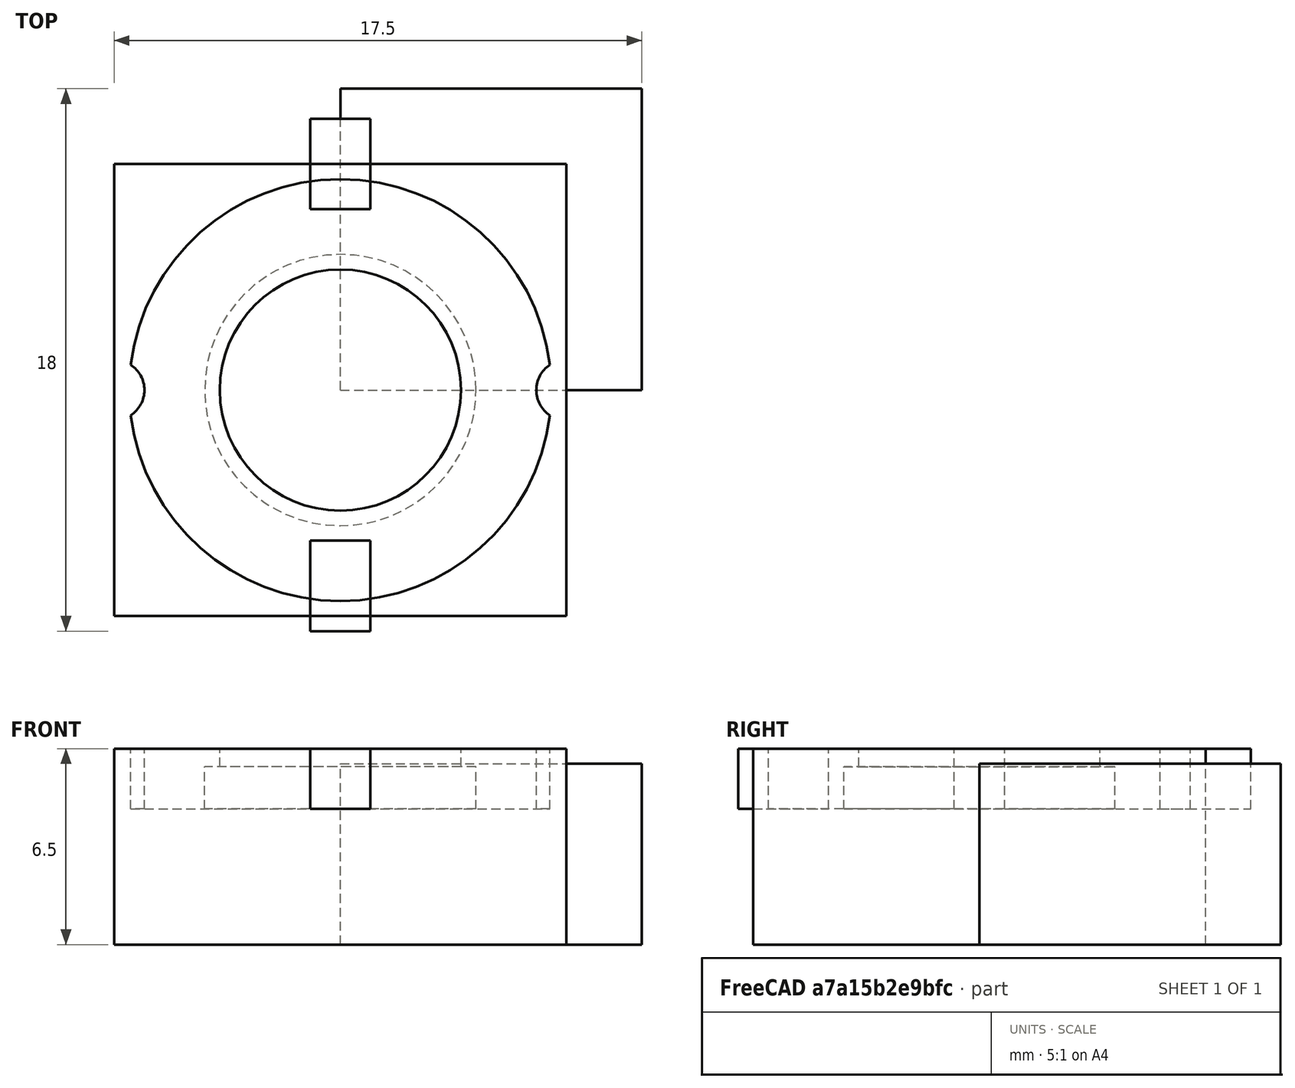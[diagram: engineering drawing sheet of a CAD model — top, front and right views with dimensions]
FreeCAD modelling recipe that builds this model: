
FCSTD DOCUMENT  (FreeCAD 0.18R16033 (Git))
Label: insulator
License: All rights reserved
LicenseURL: http://en.wikipedia.org/wiki/All_rights_reserved
objects: Part::Cylinder×5, Part::Box×4, Part::MultiFuse×1, Part::Cut×1
note: 11 computed .brp shape members not serialized (recipe doc carries the construction recipe); baked Part::Feature solids carry a one-line shape summary decoded from their .brp

FEATURE [Part::Cylinder] Cylinder  label="InnerHole"
  Angle = 360
  AttacherType = Attacher::AttachEngine3D
  Height = 1.4
  Radius = 4.5
FEATURE [Part::Cylinder] Cylinder001
  Angle = 360
  AttacherType = Attacher::AttachEngine3D
  Height = 0.6
  Placement = pos=(0,0,1.4) rot=(0,0,1;0rad)
  Radius = 4
FEATURE [Part::Cylinder] Cylinder002  label="Body"
  Angle = 360
  AttacherType = Attacher::AttachEngine3D
  Height = 2
  Radius = 7
FEATURE [Part::Cylinder] Cylinder003  label="Cylinder002"
  Angle = 360
  AttacherType = Attacher::AttachEngine3D
  Height = 10
  Placement = pos=(7.5,0,0) rot=(0,0,1;0rad)
  Radius = 1
FEATURE [Part::Cylinder] Cylinder004  label="Cylinder003"
  Angle = 360
  AttacherType = Attacher::AttachEngine3D
  Height = 10
  Placement = pos=(-7.5,0,0) rot=(0,0,1;0rad)
  Radius = 1
FEATURE [Part::MultiFuse] Fusion
  Shapes = -> [Cylinder001,Cylinder,Cylinder003,Cylinder004]
FEATURE [Part::Box] Box  label="Cube"
  AttacherType = Attacher::AttachEngine3D
  Height = 6.5
  Length = 15
  Placement = pos=(-7.5,-7.5,0) rot=(0,0,1;0rad)
  Width = 15
FEATURE [Part::Box] Box001  label="Cube001"
  AttacherType = Attacher::AttachEngine3D
  Height = 2
  Length = 2
  Placement = pos=(-1,-8,4.5) rot=(0,0,1;0rad)
  Width = 3
FEATURE [Part::Box] Box002  label="Cube002"
  AttacherType = Attacher::AttachEngine3D
  Height = 2
  Length = 2
  Placement = pos=(-1,6,4.5) rot=(0,0,1;0rad)
  Width = 3
FEATURE [Part::Cut] Cut
  Base = -> Cylinder002
  Placement = pos=(0,0,4.5) rot=(0,0,1;0rad)
  Tool = -> Fusion
FEATURE [Part::Box] Box003  label="Cube003"
  AttacherType = Attacher::AttachEngine3D
  Height = 6
  Length = 10
  Width = 10
